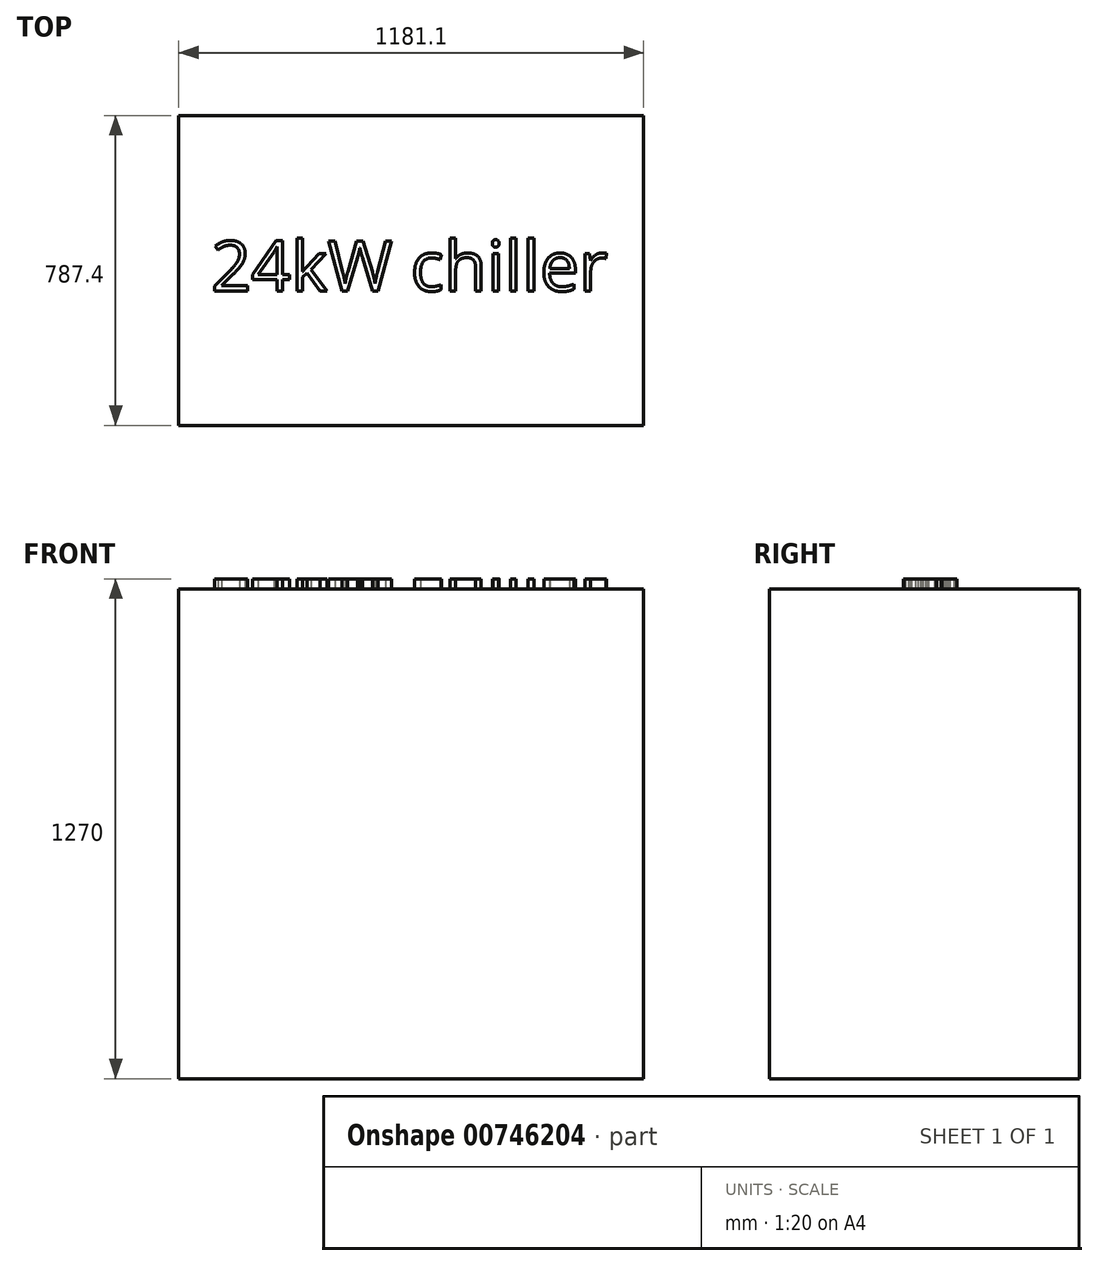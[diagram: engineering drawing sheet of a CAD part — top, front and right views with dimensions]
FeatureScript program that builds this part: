
annotation { "Feature Type Name" : "Feature", "Feature Type Description" : "" }
export const myFeature = defineFeature(function(context is Context, id is Id, definition is map)
    precondition{}
    {
        {
            var Q0;
            Q0=qCreatedBy(makeId("Top.planeOp"),FACE);
            var sketch = newSketch(context, id + "F0", { "sketchPlane" : qUnion([Q0])});
            skLineSegment(sketch, "E0.bottom", {"start": v(590.55, -393.7) * mm, "end": v(-590.55, -393.7) * mm});
            skLineSegment(sketch, "E0.top", {"start": v(590.55, 393.7) * mm, "end": v(-590.55, 393.7) * mm});
            skLineSegment(sketch, "E0.left", {"start": v(590.55, -393.7) * mm, "end": v(590.55, 393.7) * mm});
            skLineSegment(sketch, "E0.right", {"start": v(-590.55, -393.7) * mm, "end": v(-590.55, 393.7) * mm});
            skPoint(sketch, "E0.middle", {"position": v(0, 0) * mm});
            skSolve(sketch);
        }
        {
            var Q0;
            Q0=makeQuery(id+"F0.imprint","IMPRINT",FACE,{"disambiguationData":[TD([[makeQuery(id+"F0.imprint","IMPRINT",EDGE,{"derivedFrom":sQuery(id+"F0.wireOp",EDGE,"E0.bottom")}),-1.0]])]});
            extrude(context, id + "F1", {"entities" : qUnion([Q0]), "depth" : 1244.6 * mm, "offsetDistance" : 25.4 * mm});
        }
        {
            var Q0;
            Q0=makeQuery(id+"F1.opExtrude","CAP_FACE",FACE,{"disambiguationData":[OSD([sQuery(id+"F0.wireOp",EDGE,"E0.bottom"),sQuery(id+"F0.wireOp",EDGE,"E0.top"),sQuery(id+"F0.wireOp",EDGE,"E0.left"),sQuery(id+"F0.wireOp",EDGE,"E0.right")])],"isStart":false});
            var sketch = newSketch(context, id + "F2", { "sketchPlane" : qUnion([Q0])});
            skText(sketch, "E1", { "text": "24kW chiller", "fontName": "OpenSans-Regular.ttf"});
            const initialGuessF2  = {"E1": [-0.508, -0.05235, 1, 0, 0.12783]};
            skSetInitialGuess(sketch, initialGuessF2);
            skSolve(sketch);
        }
        {
            var Q0;
            Q0 = qSketchRegion(id + "F2", true);
            extrude(context, id + "F3", {"entities" : qUnion([Q0]), "operationType" : NewBodyOperationType.ADD, "depth" : 25.4 * mm, "offsetDistance" : 25.4 * mm});
        }
    });
